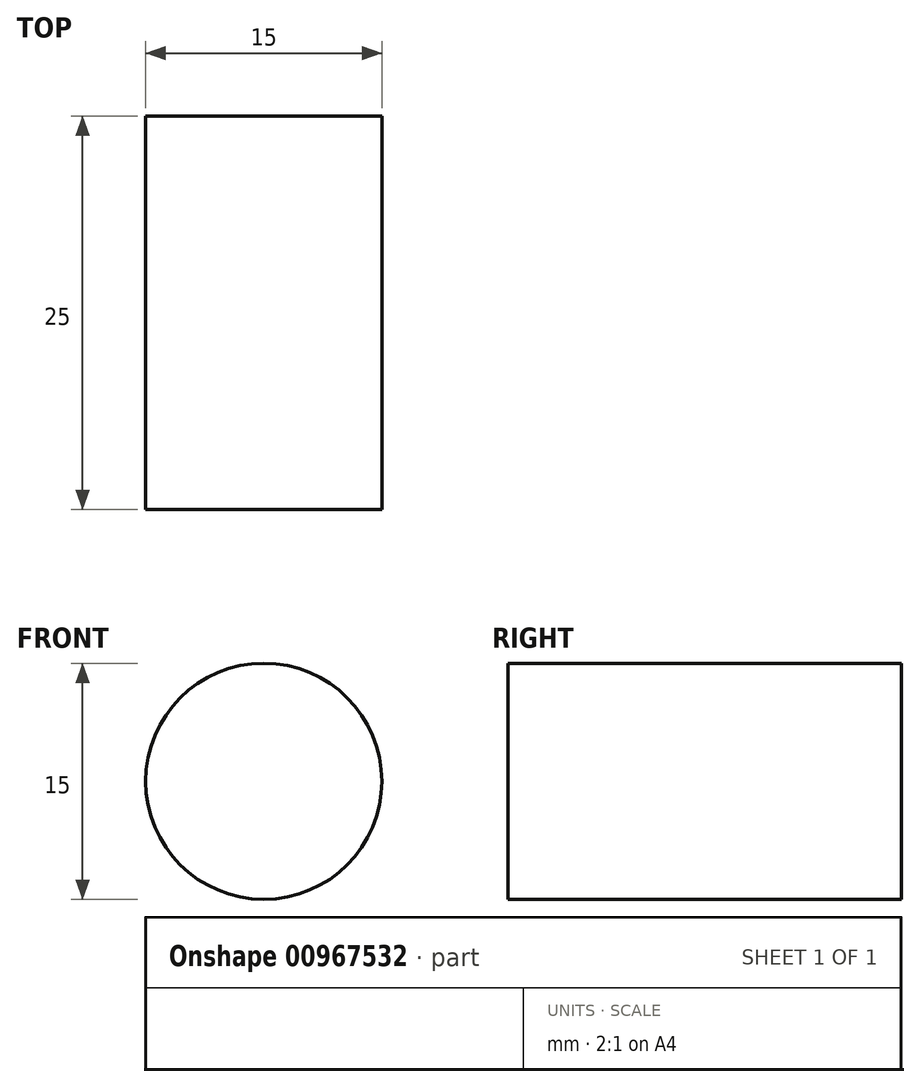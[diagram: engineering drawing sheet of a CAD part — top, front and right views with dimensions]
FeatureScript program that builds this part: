
annotation { "Feature Type Name" : "Feature", "Feature Type Description" : "" }
export const myFeature = defineFeature(function(context is Context, id is Id, definition is map)
    precondition{}
    {
        {
            var Q0;
            Q0=qCreatedBy(makeId("Front.planeOp"),FACE);
            var sketch = newSketch(context, id + "F0", { "sketchPlane" : qUnion([Q0])});
            skCircle(sketch, "E0", {"center": v(0, 0) * mm, "radius": 7.5 * mm});
            skSolve(sketch);
        }
        {
            var Q0;
            Q0=makeQuery(id+"F0.imprint","IMPRINT",FACE,{"disambiguationData":[TD([[makeQuery(id+"F0.imprint","IMPRINT",EDGE,{"derivedFrom":sQuery(id+"F0.wireOp",EDGE,"E0")}),1.0]])]});
            extrude(context, id + "F1", {"entities" : qUnion([Q0]), "depth" : 25 * mm, "offsetDistance" : 25 * mm, "symmetric" : true});
        }
    });
